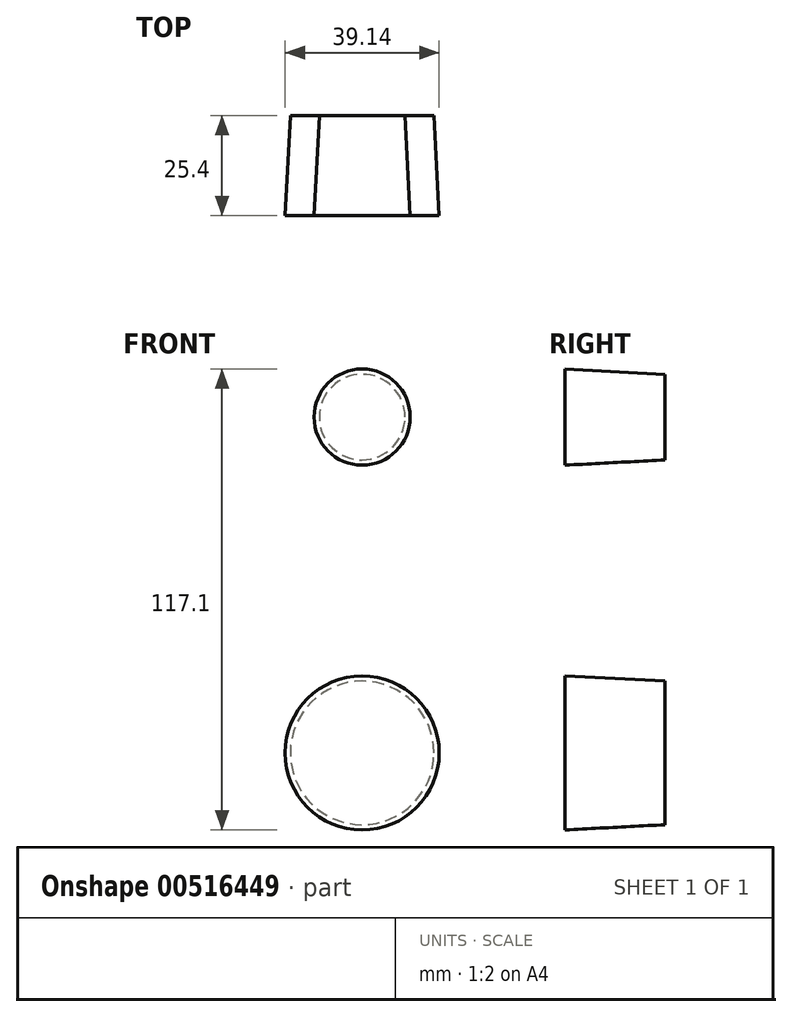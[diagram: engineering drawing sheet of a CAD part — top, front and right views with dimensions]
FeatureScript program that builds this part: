
annotation { "Feature Type Name" : "Feature", "Feature Type Description" : "" }
export const myFeature = defineFeature(function(context is Context, id is Id, definition is map)
    precondition{}
    {
        {
            var Q0;
            Q0=qCreatedBy(makeId("Front.planeOp"),FACE);
            var sketch = newSketch(context, id + "F0", { "sketchPlane" : qUnion([Q0])});
            skLineSegment(sketch, "E0", {"start": v(-10.91, 55.95) * mm, "end": v(-10.91, -14.33) * mm});
            skLineSegment(sketch, "E1", {"start": v(10.7, 56.23) * mm, "end": v(10.7, -14.33) * mm});
            skCircle(sketch, "E2", {"center": v(0, 56.23) * mm, "radius": 10.88 * mm});
            skCircle(sketch, "E3", {"center": v(0, -29.1) * mm, "radius": 18.24 * mm});
            skSolve(sketch);
        }
        {
            var Q0;
            Q0 = qSketchRegion(id + "F0", true);
            extrude(context, id + "F1", {"entities" : qUnion([Q0]), "depth" : 25.4 * mm, "offsetDistance" : 25.4 * mm, "hasDraft" : true, "draftAngle" : 3 * degree});
        }
    });
